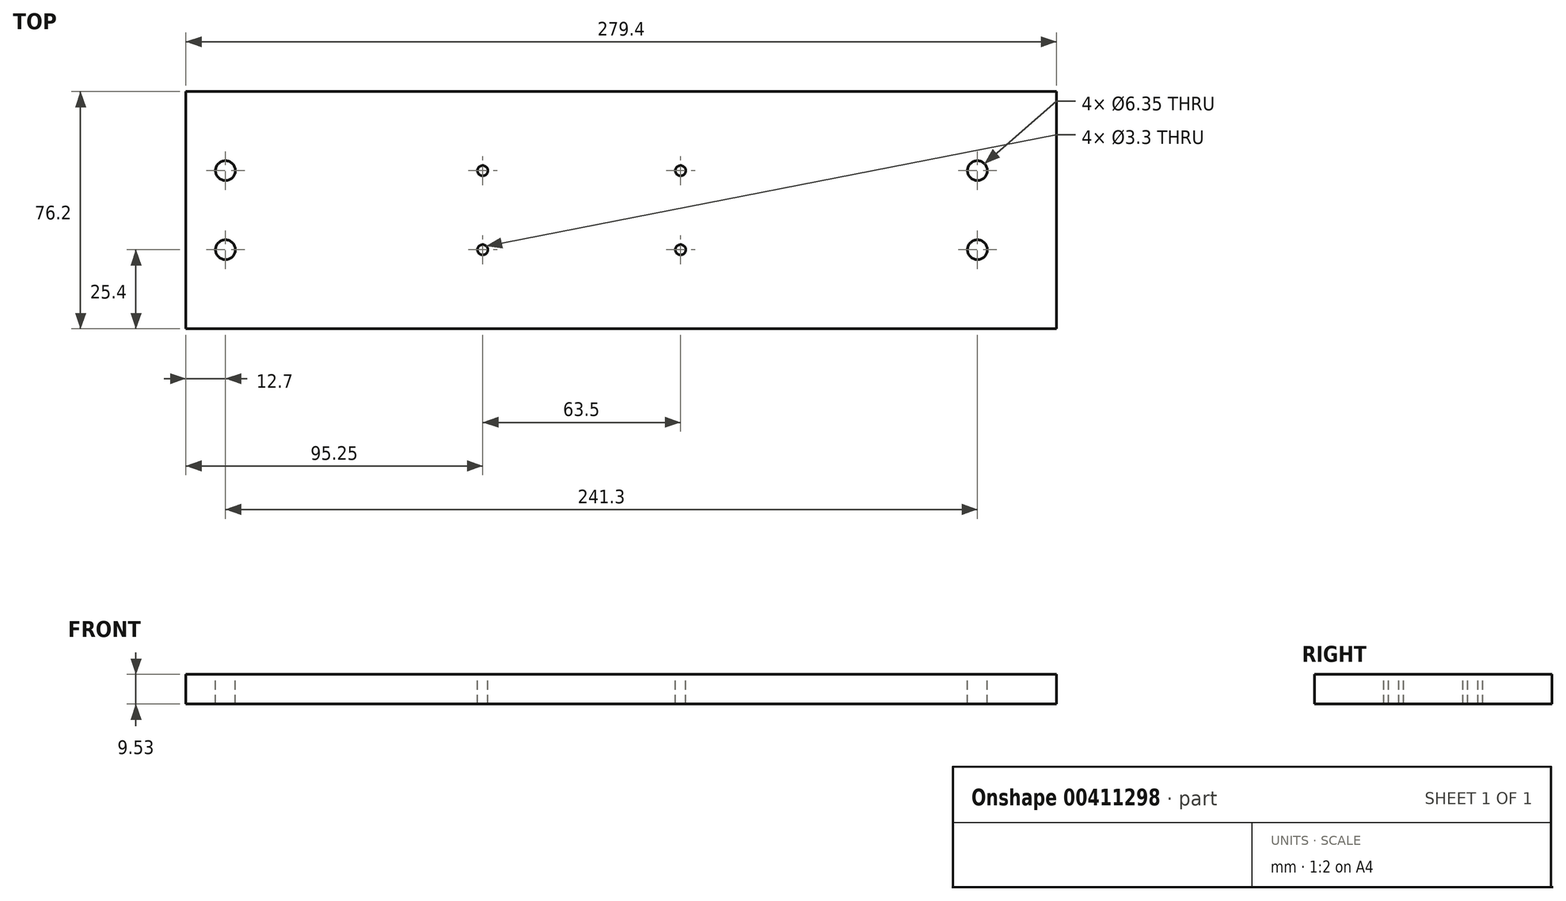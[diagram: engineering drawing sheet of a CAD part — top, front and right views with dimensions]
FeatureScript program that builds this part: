
annotation { "Feature Type Name" : "Feature", "Feature Type Description" : "" }
export const myFeature = defineFeature(function(context is Context, id is Id, definition is map)
    precondition{}
    {
        {
            var Q0;
            Q0=qCreatedBy(makeId("Top.planeOp"),FACE);
            var sketch = newSketch(context, id + "F0", { "sketchPlane" : qUnion([Q0])});
            skLineSegment(sketch, "E0.bottom", {"start": v(-152.4, 38.1) * mm, "end": v(127, 38.1) * mm});
            skLineSegment(sketch, "E0.top", {"start": v(-152.4, -38.1) * mm, "end": v(127, -38.1) * mm});
            skLineSegment(sketch, "E0.left", {"start": v(-152.4, 38.1) * mm, "end": v(-152.4, -38.1) * mm});
            skLineSegment(sketch, "E0.right", {"start": v(127, 38.1) * mm, "end": v(127, -38.1) * mm});
            skSolve(sketch);
        }
        {
            var Q0;
            Q0 = qSketchRegion(id + "F0", true);
            extrude(context, id + "F1", {"entities" : qUnion([Q0]), "depth" : 9.52 * mm});
        }
        {
            var Q0;
            Q0=makeQuery(id+"F1.opExtrude","CAP_FACE",FACE,{"disambiguationData":[OSD([sQuery(id+"F0.wireOp",EDGE,"E0.bottom"),sQuery(id+"F0.wireOp",EDGE,"E0.top"),sQuery(id+"F0.wireOp",EDGE,"E0.left"),sQuery(id+"F0.wireOp",EDGE,"E0.right")])],"isStart":false});
            var sketch = newSketch(context, id + "F2", { "sketchPlane" : qUnion([Q0])});
            skCircle(sketch, "E1", {"center": v(-139.7, 12.7) * mm, "radius": 3.18 * mm});
            skCircle(sketch, "E2", {"center": v(-139.7, -12.7) * mm, "radius": 3.18 * mm});
            skCircle(sketch, "E3", {"center": v(101.6, 12.7) * mm, "radius": 3.18 * mm});
            skCircle(sketch, "E4", {"center": v(101.6, -12.7) * mm, "radius": 3.18 * mm});
            skCircle(sketch, "E5", {"center": v(-57.15, 12.7) * mm, "radius": 1.65 * mm});
            skCircle(sketch, "E6", {"center": v(6.35, 12.7) * mm, "radius": 1.65 * mm});
            skCircle(sketch, "E7", {"center": v(6.35, -12.7) * mm, "radius": 1.65 * mm});
            skCircle(sketch, "E8", {"center": v(-57.15, -12.7) * mm, "radius": 1.65 * mm});
            skSolve(sketch);
        }
        {
            var Q0;
            Q0 = qSketchRegion(id + "F2", true);
            extrude(context, id + "F3", {"entities" : qUnion([Q0]), "operationType" : NewBodyOperationType.REMOVE, "endBound" : BoundingType.THROUGH_ALL, "oppositeDirection" : true, "depth" : 25.4 * mm});
        }
    });
